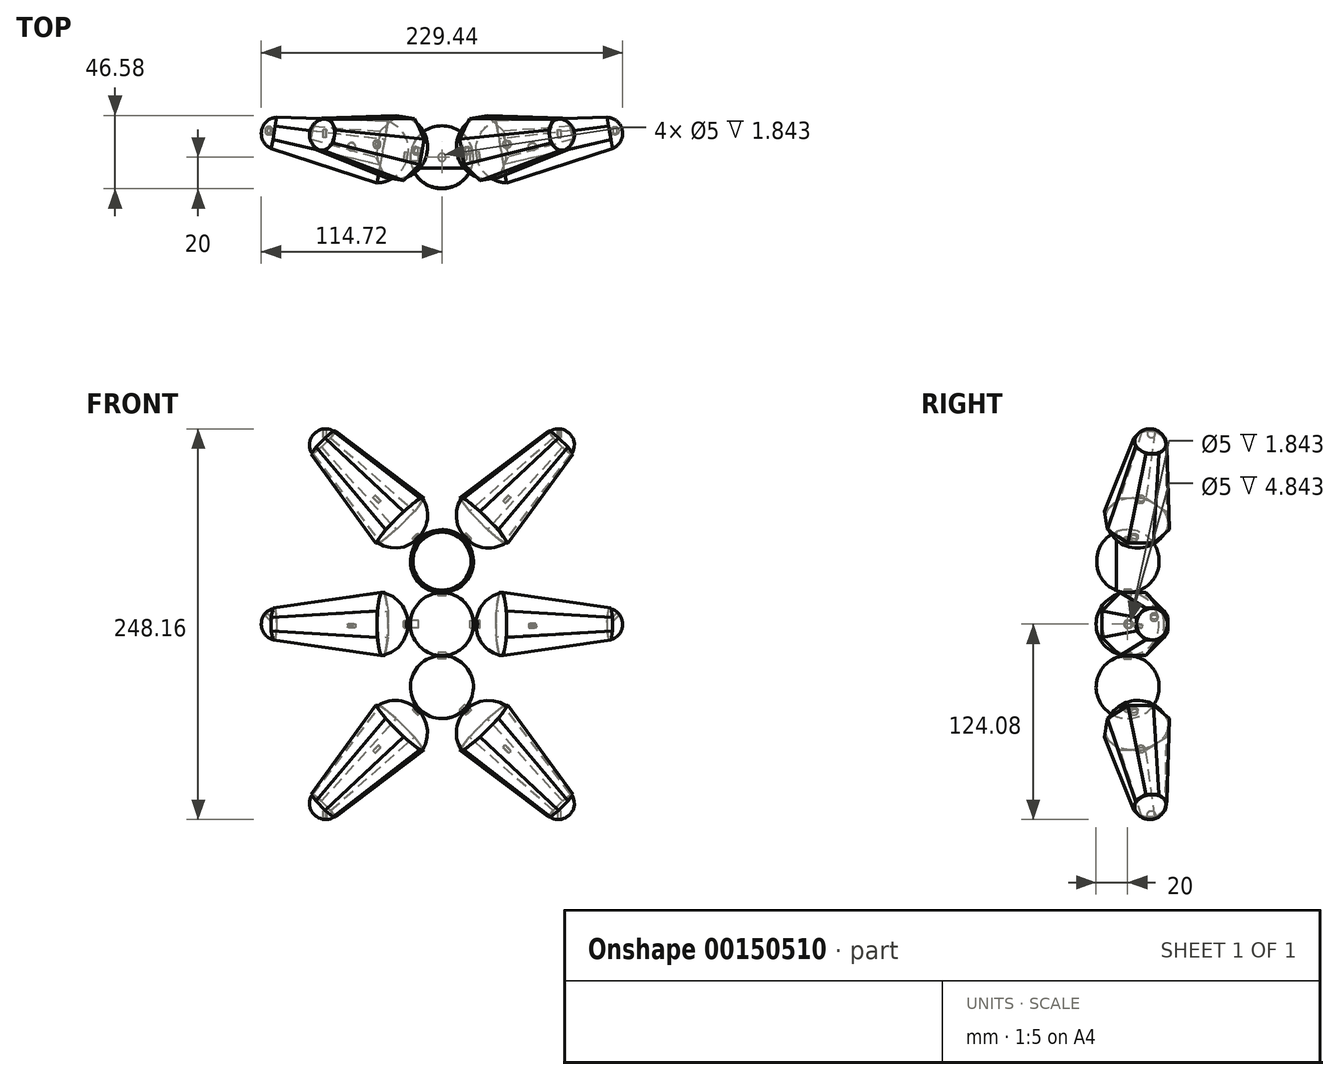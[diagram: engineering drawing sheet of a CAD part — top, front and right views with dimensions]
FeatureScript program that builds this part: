
annotation { "Feature Type Name" : "Feature", "Feature Type Description" : "" }
export const myFeature = defineFeature(function(context is Context, id is Id, definition is map)
    precondition{}
    {
        {
            var Q0;
            Q0=qCreatedBy(makeId("Top.planeOp"),FACE);
            var sketch = newSketch(context, id + "F0", { "sketchPlane" : qUnion([Q0])});
            skCircle(sketch, "E0", {"center": v(0, 0) * mm, "radius": 20 * mm});
            skCircle(sketch, "E1.cCircle", {"center": v(0, 0) * mm, "radius": 20 * mm, "construction": true});
            skLineSegment(sketch, "E1.0", {"start": v(18.28, 11.6) * mm, "end": v(21.13, -4.72) * mm});
            skLineSegment(sketch, "E1.1", {"start": v(21.13, -4.72) * mm, "end": v(11.6, -18.28) * mm});
            skLineSegment(sketch, "E1.2", {"start": v(11.6, -18.28) * mm, "end": v(-4.72, -21.13) * mm});
            skLineSegment(sketch, "E1.3", {"start": v(-4.72, -21.13) * mm, "end": v(-18.28, -11.6) * mm});
            skLineSegment(sketch, "E1.4", {"start": v(-18.28, -11.6) * mm, "end": v(-21.13, 4.72) * mm});
            skLineSegment(sketch, "E1.5", {"start": v(-21.13, 4.72) * mm, "end": v(-11.6, 18.28) * mm});
            skLineSegment(sketch, "E1.6", {"start": v(-11.6, 18.28) * mm, "end": v(4.72, 21.13) * mm});
            skLineSegment(sketch, "E1.7", {"start": v(4.72, 21.13) * mm, "end": v(18.28, 11.6) * mm});
            skPoint(sketch, "E1.0.midPoint", {"position": v(19.7, 3.44) * mm});
            skSolve(sketch);
        }
        {
            var Q0;
            {var subQ0=sQuery(id+"F0.wireOp",EDGE,"E0");var subQ4=makeQuery(id+"F0.imprint","INTERSECT",VERTEX,{"derivedFrom":[subQ0,sQuery(id+"F0.wireOp",EDGE,"E1.7")]});Q0=makeQuery(id+"F0.imprint","IMPRINT",FACE,{"disambiguationData":[TD([[makeQuery(id+"F0.imprint","IMPRINT",EDGE,{"disambiguationData":[TD([[subQ4,1.0]])],"derivedFrom":subQ0}),1.0]])]});}
            extrude(context, id + "F1", {"entities" : qUnion([Q0]), "oppositeDirection" : true, "depth" : 16 * mm});
        }
        {
            var Q0;
            {var subQ0=sQuery(id+"F0.wireOp",EDGE,"E0");var subQ4=makeQuery(id+"F0.imprint","INTERSECT",VERTEX,{"derivedFrom":[subQ0,sQuery(id+"F0.wireOp",EDGE,"E1.7")]});Q0=makeQuery(id+"F0.imprint","IMPRINT",FACE,{"disambiguationData":[TD([[makeQuery(id+"F0.imprint","IMPRINT",EDGE,{"disambiguationData":[TD([[subQ4,1.0]])],"derivedFrom":subQ0}),1.0]])]});}
            var Q1;
            {var subQ0=sQuery(id+"F0.wireOp",EDGE,"E1.7");var subQ1=sQuery(id+"F0.wireOp",EDGE,"E0");var subQ2=makeQuery(id+"F0.imprint","INTERSECT",VERTEX,{"derivedFrom":[subQ1,subQ0]});Q1=makeQuery(id+"F0.imprint","IMPRINT",FACE,{"disambiguationData":[TD([[makeQuery(id+"F0.imprint","IMPRINT",EDGE,{"disambiguationData":[TD([[subQ2,-1.0]])],"derivedFrom":subQ1}),-1.0]])]});}
            var Q2;
            {var subQ0=sQuery(id+"F0.wireOp",EDGE,"E1.7");var subQ1=sQuery(id+"F0.wireOp",EDGE,"E0");var subQ2=makeQuery(id+"F0.imprint","INTERSECT",VERTEX,{"derivedFrom":[subQ1,subQ0]});Q2=makeQuery(id+"F0.imprint","IMPRINT",FACE,{"disambiguationData":[TD([[makeQuery(id+"F0.imprint","IMPRINT",EDGE,{"disambiguationData":[TD([[subQ2,1.0]])],"derivedFrom":subQ1}),-1.0]])]});}
            var Q3;
            {var subQ0=sQuery(id+"F0.wireOp",EDGE,"E1.0");var subQ1=sQuery(id+"F0.wireOp",EDGE,"E0");var subQ2=makeQuery(id+"F0.imprint","INTERSECT",VERTEX,{"derivedFrom":[subQ1,subQ0]});Q3=makeQuery(id+"F0.imprint","IMPRINT",FACE,{"disambiguationData":[TD([[makeQuery(id+"F0.imprint","IMPRINT",EDGE,{"disambiguationData":[TD([[subQ2,1.0]])],"derivedFrom":subQ1}),-1.0]])]});}
            var Q4;
            {var subQ0=sQuery(id+"F0.wireOp",EDGE,"E1.2");var subQ1=sQuery(id+"F0.wireOp",EDGE,"E0");var subQ2=makeQuery(id+"F0.imprint","INTERSECT",VERTEX,{"derivedFrom":[subQ1,subQ0]});Q4=makeQuery(id+"F0.imprint","IMPRINT",FACE,{"disambiguationData":[TD([[makeQuery(id+"F0.imprint","IMPRINT",EDGE,{"disambiguationData":[TD([[subQ2,-1.0]])],"derivedFrom":subQ1}),-1.0]])]});}
            var Q5;
            {var subQ0=sQuery(id+"F0.wireOp",EDGE,"E1.3");var subQ1=sQuery(id+"F0.wireOp",EDGE,"E0");var subQ2=makeQuery(id+"F0.imprint","INTERSECT",VERTEX,{"derivedFrom":[subQ1,subQ0]});Q5=makeQuery(id+"F0.imprint","IMPRINT",FACE,{"disambiguationData":[TD([[makeQuery(id+"F0.imprint","IMPRINT",EDGE,{"disambiguationData":[TD([[subQ2,-1.0]])],"derivedFrom":subQ1}),-1.0]])]});}
            var Q6;
            {var subQ0=sQuery(id+"F0.wireOp",EDGE,"E1.4");var subQ1=sQuery(id+"F0.wireOp",EDGE,"E0");var subQ2=makeQuery(id+"F0.imprint","INTERSECT",VERTEX,{"derivedFrom":[subQ1,subQ0]});Q6=makeQuery(id+"F0.imprint","IMPRINT",FACE,{"disambiguationData":[TD([[makeQuery(id+"F0.imprint","IMPRINT",EDGE,{"disambiguationData":[TD([[subQ2,-1.0]])],"derivedFrom":subQ1}),-1.0]])]});}
            var Q7;
            {var subQ0=sQuery(id+"F0.wireOp",EDGE,"E1.5");var subQ1=sQuery(id+"F0.wireOp",EDGE,"E0");var subQ2=makeQuery(id+"F0.imprint","INTERSECT",VERTEX,{"derivedFrom":[subQ1,subQ0]});Q7=makeQuery(id+"F0.imprint","IMPRINT",FACE,{"disambiguationData":[TD([[makeQuery(id+"F0.imprint","IMPRINT",EDGE,{"disambiguationData":[TD([[subQ2,-1.0]])],"derivedFrom":subQ1}),-1.0]])]});}
            var Q8;
            {var subQ0=sQuery(id+"F0.wireOp",EDGE,"E1.6");var subQ1=sQuery(id+"F0.wireOp",EDGE,"E0");var subQ2=makeQuery(id+"F0.imprint","INTERSECT",VERTEX,{"derivedFrom":[subQ1,subQ0]});Q8=makeQuery(id+"F0.imprint","IMPRINT",FACE,{"disambiguationData":[TD([[makeQuery(id+"F0.imprint","IMPRINT",EDGE,{"disambiguationData":[TD([[subQ2,-1.0]])],"derivedFrom":subQ1}),-1.0]])]});}
            extrude(context, id + "F2", {"entities" : qUnion([Q0, Q1, Q2, Q3, Q4, Q5, Q6, Q7, Q8]), "operationType" : NewBodyOperationType.ADD, "depth" : 70 * mm, "hasDraft" : true, "draftAngle" : 8 * degree, "draftPullDirection" : true});
        }
        {
            var Q0;
            Q0=makeQuery(id+"F1.opExtrude","CAP_EDGE",EDGE,{"disambiguationData":[OSD([sQuery(id+"F0.wireOp",EDGE,"E0")])],"isStart":false});
            fillet(context, id + "F3", {"entities" : qUnion([Q0]), "radius" : 20 * mm, "tangentPropagation" : true, "allowEdgeOverflow" : false});
        }
        {
            var Q0;
            Q0=makeQuery(id+"F2.opExtrude","CAP_FACE",FACE,{"disambiguationData":[OSD([sQuery(id+"F0.wireOp",EDGE,"E1.0"),sQuery(id+"F0.wireOp",EDGE,"E1.1"),sQuery(id+"F0.wireOp",EDGE,"E1.2"),sQuery(id+"F0.wireOp",EDGE,"E1.3"),sQuery(id+"F0.wireOp",EDGE,"E1.4"),sQuery(id+"F0.wireOp",EDGE,"E1.5"),sQuery(id+"F0.wireOp",EDGE,"E1.6"),sQuery(id+"F0.wireOp",EDGE,"E1.7")])],"isStart":false});
            var sketch = newSketch(context, id + "F4", { "sketchPlane" : qUnion([Q0])});
            skCircle(sketch, "E2", {"center": v(0, 0) * mm, "radius": 10 * mm});
            skSolve(sketch);
        }
        {
            var Q0;
            Q0=makeQuery(id+"F4.imprint","IMPRINT",FACE,{"disambiguationData":[TD([[makeQuery(id+"F4.imprint","IMPRINT",EDGE,{"derivedFrom":sQuery(id+"F4.wireOp",EDGE,"E2")}),1.0]])]});
            extrude(context, id + "F5", {"entities" : qUnion([Q0]), "operationType" : NewBodyOperationType.ADD, "depth" : 8 * mm});
        }
        {
            var Q0;
            Q0=makeQuery(id+"F5.opExtrude","CAP_EDGE",EDGE,{"disambiguationData":[OSD([sQuery(id+"F4.wireOp",EDGE,"E2")])],"isStart":false});
            fillet(context, id + "F6", {"entities" : qUnion([Q0]), "radius" : 10 * mm, "tangentPropagation" : true, "allowEdgeOverflow" : false});
        }
        {
            var Q0;
            Q0=makeQuery(id+"F1.opExtrude","CAP_FACE",FACE,{"disambiguationData":[OSD([sQuery(id+"F0.wireOp",EDGE,"E0")])],"isStart":false});
            var sketch = newSketch(context, id + "F7", { "sketchPlane" : qUnion([Q0])});
            skCircle(sketch, "E3", {"center": v(0, 0) * mm, "radius": 2.5 * mm});
            skSolve(sketch);
        }
        {
            var Q0;
            Q0 = qSketchRegion(id + "F7", true);
            extrude(context, id + "F8", {"entities" : qUnion([Q0]), "operationType" : NewBodyOperationType.REMOVE, "oppositeDirection" : true, "depth" : 2 * mm});
        }
        {
            var Q0;
            {var subQ0=sQuery(id+"F0.wireOp",EDGE,"E0");var subQ4=makeQuery(id+"F0.imprint","INTERSECT",VERTEX,{"derivedFrom":[subQ0,sQuery(id+"F0.wireOp",EDGE,"E1.7")]});Q0=makeQuery(id+"F0.imprint","IMPRINT",FACE,{"disambiguationData":[TD([[makeQuery(id+"F0.imprint","IMPRINT",EDGE,{"disambiguationData":[TD([[subQ4,1.0]])],"derivedFrom":subQ0}),1.0]])]});}
            extrude(context, id + "F9", {"entities" : qUnion([Q0]), "endBound" : BoundingType.SYMMETRIC, "depth" : 40 * mm});
        }
        {
            var Q0;
            Q0=makeQuery(id+"F9.opExtrude","CAP_EDGE",EDGE,{"disambiguationData":[OSD([sQuery(id+"F0.wireOp",EDGE,"E0")])],"isStart":false});
            var Q1;
            Q1=makeQuery(id+"F9.opExtrude","CAP_EDGE",EDGE,{"disambiguationData":[OSD([sQuery(id+"F0.wireOp",EDGE,"E0")])],"isStart":true});
            fillet(context, id + "F10", {"entities" : qUnion([Q0, Q1]), "radius" : 20 * mm, "tangentPropagation" : true, "allowEdgeOverflow" : false});
        }
        {
            var Q0;
            Q0=makeQuery(id+"F1.opExtrude","SWEPT_BODY",BODY,{"disambiguationData":[OSD([sQuery(id+"F0.wireOp",EDGE,"E0")])]});
            transform(context, id + "F11", {"entities" : qUnion([Q0]), "transformType" : TransformType.TRANSLATION_3D, "dx" : 18 * mm, "dy" : 0 * mm, "dz" : -20 * mm, "makeCopy" : false});
        }
        {
            var Q0;
            Q0=makeQuery(id+"F9.opExtrude","SWEPT_BODY",BODY,{"disambiguationData":[OSD([sQuery(id+"F0.wireOp",EDGE,"E0")])]});
            transform(context, id + "F12", {"entities" : qUnion([Q0]), "transformType" : TransformType.TRANSLATION_3D, "dx" : 0 * mm, "dy" : 0 * mm, "dz" : 40 * mm, "makeCopy" : false});
        }
        {
            var Q0;
            Q0=qCreatedBy(makeId("Top.planeOp"),FACE);
            cPlane(context, id + "F13", {"entities" : qUnion([Q0]), "cplaneType" : CPlaneType.OFFSET, "offset" : 20 * mm, "width" : 150 * mm, "height" : 150 * mm});
        }
        {
            var Q0;
            Q0=qCreatedBy(id+"F13.planeOp",FACE);
            var sketch = newSketch(context, id + "F14", { "sketchPlane" : qUnion([Q0])});
            skCircle(sketch, "E4", {"center": v(0, 0) * mm, "radius": 2.5 * mm});
            skSolve(sketch);
        }
        {
            var Q0;
            Q0 = qSketchRegion(id + "F14", true);
            extrude(context, id + "F15", {"entities" : qUnion([Q0]), "operationType" : NewBodyOperationType.REMOVE, "depth" : 2 * mm});
        }
        {
            var Q0;
            Q0=makeQuery(id+"F9.opExtrude","SWEPT_BODY",BODY,{"disambiguationData":[OSD([sQuery(id+"F0.wireOp",EDGE,"E0")])]});
            transform(context, id + "F16", {"entities" : qUnion([Q0]), "transformType" : TransformType.TRANSLATION_3D, "dx" : 0 * mm, "dy" : 0 * mm, "dz" : -40 * mm, "makeCopy" : true});
        }
        {
            var Q0;
            Q0=qCreatedBy(makeId("Front.planeOp"),FACE);
            var sketch = newSketch(context, id + "F17", { "sketchPlane" : qUnion([Q0])});
            skLineSegment(sketch, "E5", {"start": v(0, 68.28) * mm, "end": v(-28.28, 40) * mm});
            skLineSegment(sketch, "E6", {"start": v(-28.28, 40) * mm, "end": v(0, 11.72) * mm});
            skLineSegment(sketch, "E7", {"start": v(0, 11.72) * mm, "end": v(28.28, 40) * mm});
            skLineSegment(sketch, "E8", {"start": v(28.28, 40) * mm, "end": v(0, 68.28) * mm});
            skLineSegment(sketch, "E9", {"start": v(0, 0) * mm, "end": v(0, 68.28) * mm, "construction": true});
            skLineSegment(sketch, "E10", {"start": v(-28.28, 40) * mm, "end": v(28.28, 40) * mm, "construction": true});
            skSolve(sketch);
        }
        {
            var Q0;
            Q0=sQuery(id+"F17.wireOp",EDGE,"E5");
            cPlane(context, id + "F18", {"entities" : qUnion([Q0]), "cplaneType" : CPlaneType.LINE_ANGLE, "offset" : 25 * mm, "angle" : 90 * degree, "width" : 150 * mm, "height" : 150 * mm});
        }
        {
            var Q0;
            Q0=qCreatedBy(id+"F18.planeOp",FACE);
            var sketch = newSketch(context, id + "F19", { "sketchPlane" : qUnion([Q0])});
            skCircle(sketch, "E11", {"center": v(28.28, 0) * mm, "radius": 2.5 * mm});
            skSolve(sketch);
        }
        {
            var Q0;
            Q0 = qSketchRegion(id + "F19", true);
            extrude(context, id + "F20", {"entities" : qUnion([Q0]), "operationType" : NewBodyOperationType.REMOVE, "oppositeDirection" : true, "depth" : 2 * mm});
        }
        {
            var Q0;
            Q0=sQuery(id+"F17.wireOp",EDGE,"E8");
            cPlane(context, id + "F21", {"entities" : qUnion([Q0]), "cplaneType" : CPlaneType.LINE_ANGLE, "offset" : 25 * mm, "angle" : 90 * degree, "width" : 150 * mm, "height" : 150 * mm});
        }
        {
            var Q0;
            Q0=qCreatedBy(id+"F21.planeOp",FACE);
            var sketch = newSketch(context, id + "F22", { "sketchPlane" : qUnion([Q0])});
            skCircle(sketch, "E12", {"center": v(0, 28.28) * mm, "radius": 2.5 * mm});
            skSolve(sketch);
        }
        {
            var Q0;
            Q0 = qSketchRegion(id + "F22", true);
            extrude(context, id + "F23", {"entities" : qUnion([Q0]), "operationType" : NewBodyOperationType.REMOVE, "oppositeDirection" : true, "depth" : 2 * mm});
        }
        {
            var Q0;
            Q0=makeQuery(id+"F9.opExtrude","SWEPT_BODY",BODY,{"disambiguationData":[OSD([sQuery(id+"F0.wireOp",EDGE,"E0")])]});
            var Q1;
            Q1=qCreatedBy(makeId("Top.planeOp"),FACE);
            mirror(context, id + "F24", {"entities" : qUnion([Q0]), "mirrorPlane" : qUnion([Q1])});
        }
        {
            var Q0;
            Q0 = qSketchRegion(id + "F14", true);
            extrude(context, id + "F25", {"entities" : qUnion([Q0]), "operationType" : NewBodyOperationType.REMOVE, "oppositeDirection" : true, "depth" : 2 * mm});
        }
        {
            var Q0;
            Q0=qCreatedBy(makeId("Right.planeOp"),FACE);
            cPlane(context, id + "F26", {"entities" : qUnion([Q0]), "cplaneType" : CPlaneType.OFFSET, "offset" : 20 * mm, "width" : 150 * mm, "height" : 150 * mm});
        }
        {
            var Q0;
            Q0=qCreatedBy(id+"F26.planeOp",FACE);
            var sketch = newSketch(context, id + "F27", { "sketchPlane" : qUnion([Q0])});
            skCircle(sketch, "E13", {"center": v(0, 0) * mm, "radius": 2.5 * mm});
            skSolve(sketch);
        }
        {
            var Q0;
            Q0 = qSketchRegion(id + "F27", true);
            extrude(context, id + "F28", {"entities" : qUnion([Q0]), "operationType" : NewBodyOperationType.REMOVE, "oppositeDirection" : true, "depth" : 2 * mm});
        }
        {
            var Q0;
            Q0=qCreatedBy(makeId("Right.planeOp"),FACE);
            cPlane(context, id + "F29", {"entities" : qUnion([Q0]), "cplaneType" : CPlaneType.OFFSET, "offset" : 20 * mm, "oppositeDirection" : true, "width" : 150 * mm, "height" : 150 * mm});
        }
        {
            var Q0;
            Q0=qCreatedBy(id+"F29.planeOp",FACE);
            var sketch = newSketch(context, id + "F30", { "sketchPlane" : qUnion([Q0])});
            skCircle(sketch, "E14", {"center": v(0, 0) * mm, "radius": 2.5 * mm});
            skSolve(sketch);
        }
        {
            var Q0;
            Q0 = qSketchRegion(id + "F30", true);
            extrude(context, id + "F31", {"entities" : qUnion([Q0]), "operationType" : NewBodyOperationType.REMOVE, "depth" : 5 * mm});
        }
        {
            var Q0;
            Q0=qCreatedBy(makeId("Front.planeOp"),FACE);
            cPlane(context, id + "F32", {"entities" : qUnion([Q0]), "cplaneType" : CPlaneType.OFFSET, "offset" : 7 * mm, "width" : 150 * mm, "height" : 150 * mm});
        }
        {
            var Q0;
            Q0=qCreatedBy(id+"F32.planeOp",FACE);
            var sketch = newSketch(context, id + "F33", { "sketchPlane" : qUnion([Q0])});
            skCircle(sketch, "E15", {"center": v(0, 40) * mm, "radius": 19 * mm});
            skSolve(sketch);
        }
        {
            var Q0;
            Q0=makeQuery(id+"F33.imprint","IMPRINT",FACE,{"disambiguationData":[TD([[makeQuery(id+"F33.imprint","IMPRINT",EDGE,{"derivedFrom":sQuery(id+"F33.wireOp",EDGE,"E15")}),1.0]])]});
            extrude(context, id + "F34", {"entities" : qUnion([Q0]), "depth" : (20 - 7) * mm});
        }
        {
            var Q0;
            Q0=makeQuery(id+"F34.opExtrude","CAP_EDGE",EDGE,{"disambiguationData":[OSD([sQuery(id+"F33.wireOp",EDGE,"E15")])],"isStart":false});
            fillet(context, id + "F35", {"entities" : qUnion([Q0]), "radius" : 19 * mm, "tangentPropagation" : true, "allowEdgeOverflow" : false});
        }
        {
            var Q0;
            Q0=makeQuery(id+"F34.opExtrude","CAP_FACE",FACE,{"disambiguationData":[OSD([sQuery(id+"F33.wireOp",EDGE,"E15")])],"isStart":true});
            shell(context, id + "F36", {"entities" : qUnion([Q0]), "thickness" : .5 * mm});
        }
        {
            var Q0;
            Q0=makeQuery(id+"F34.opExtrude","SWEPT_BODY",BODY,{"disambiguationData":[OSD([sQuery(id+"F33.wireOp",EDGE,"E15")])]});
            var Q1;
            Q1=makeQuery(id+"F9.opExtrude","SWEPT_BODY",BODY,{"disambiguationData":[OSD([sQuery(id+"F0.wireOp",EDGE,"E0")])]});
            booleanBodies(context, id + "F37", {"operationType" : BooleanOperationType.SUBTRACTION, "tools" : qUnion([Q0]), "targets" : qUnion([Q1])});
        }
        {
            var Q0;
            Q0=makeQuery(id+"F1.opExtrude","SWEPT_BODY",BODY,{"disambiguationData":[OSD([sQuery(id+"F0.wireOp",EDGE,"E0")])]});
            var Q1;
            {var subQ0=sQuery(id+"F0.wireOp",EDGE,"E1.2");var subQ1=sQuery(id+"F0.wireOp",EDGE,"E1.3");Q1=makeQuery(id+"F2.boolean.opBoolean","SPLIT",EDGE,{"disambiguationData":[TD([makeQuery(id+"F2.opExtrude","SWEPT_FACE",FACE,{"disambiguationData":[OSD([subQ1])]})])],"derivedFrom":makeQuery(id+"F2.opExtrude","CAP_EDGE",EDGE,{"disambiguationData":[OSD([subQ0])],"isStart":true})});}
            var Q2;
            {var subQ0=sQuery(id+"F0.wireOp",EDGE,"E1.0");var subQ1=sQuery(id+"F0.wireOp",EDGE,"E1.7");Q2=makeQuery(id+"F2.boolean.opBoolean","SPLIT",EDGE,{"disambiguationData":[TD([makeQuery(id+"F2.opExtrude","SWEPT_FACE",FACE,{"disambiguationData":[OSD([subQ1])]})])],"derivedFrom":makeQuery(id+"F2.opExtrude","CAP_EDGE",EDGE,{"disambiguationData":[OSD([subQ0])],"isStart":true})});}
            transform(context, id + "F38", {"entities" : qUnion([Q0]), "transformType" : TransformType.ROTATION, "transformAxis" : qUnion([Q2]), "angle" : 90 * degree, "oppositeDirection" : true, "makeCopy" : false});
        }
        {
            var Q0;
            Q0=makeQuery(id+"F1.opExtrude","SWEPT_BODY",BODY,{"disambiguationData":[OSD([sQuery(id+"F0.wireOp",EDGE,"E0")])]});
            var Q1;
            Q1=qCreatedBy(makeId("Right.planeOp"),FACE);
            mirror(context, id + "F39", {"entities" : qUnion([Q0]), "mirrorPlane" : qUnion([Q1])});
        }
        {
            var Q0;
            Q0=makeQuery(id+"F1.opExtrude","SWEPT_BODY",BODY,{"disambiguationData":[OSD([sQuery(id+"F0.wireOp",EDGE,"E0")])]});
            transform(context, id + "F40", {"entities" : qUnion([Q0]), "transformType" : TransformType.TRANSLATION_3D, "dx" : -25 * mm, "dy" : 0 * mm, "dz" : 60 * mm, "makeCopy" : true});
        }
        {
            var Q0;
            Q0=makeQuery(id+"F40.opPattern","COPY",BODY,{"derivedFrom":makeQuery(id+"F1.opExtrude","SWEPT_BODY",BODY,{"disambiguationData":[OSD([sQuery(id+"F0.wireOp",EDGE,"E0")])]}),"instanceName":"1"});
            var Q1;
            {var subQ0=sQuery(id+"F0.wireOp",EDGE,"E1.5");var subQ1=sQuery(id+"F0.wireOp",EDGE,"E1.4");Q1=makeQuery(id+"F40.opPattern","COPY",EDGE,{"derivedFrom":makeQuery(id+"F2.boolean.opBoolean","SPLIT",EDGE,{"disambiguationData":[TD([makeQuery(id+"F2.opExtrude","SWEPT_FACE",FACE,{"disambiguationData":[OSD([subQ0])]})])],"derivedFrom":makeQuery(id+"F2.opExtrude","CAP_EDGE",EDGE,{"disambiguationData":[OSD([subQ1])],"isStart":true})}),"instanceName":"1"});}
            transform(context, id + "F41", {"entities" : qUnion([Q0]), "transformType" : TransformType.ROTATION, "transformAxis" : qUnion([Q1]), "angle" : 45 * degree, "oppositeDirection" : true, "makeCopy" : false});
        }
        {
            var Q0;
            Q0=makeQuery(id+"F40.opPattern","COPY",BODY,{"derivedFrom":makeQuery(id+"F1.opExtrude","SWEPT_BODY",BODY,{"disambiguationData":[OSD([sQuery(id+"F0.wireOp",EDGE,"E0")])]}),"instanceName":"1"});
            var Q1;
            Q1=qCreatedBy(makeId("Right.planeOp"),FACE);
            mirror(context, id + "F42", {"entities" : qUnion([Q0]), "mirrorPlane" : qUnion([Q1])});
        }
        {
            var Q0;
            Q0=makeQuery(id+"F42.opPattern","COPY",BODY,{"derivedFrom":makeQuery(id+"F40.opPattern","COPY",BODY,{"derivedFrom":makeQuery(id+"F1.opExtrude","SWEPT_BODY",BODY,{"disambiguationData":[OSD([sQuery(id+"F0.wireOp",EDGE,"E0")])]}),"instanceName":"1"}),"instanceName":"1"});
            var Q1;
            Q1=makeQuery(id+"F40.opPattern","COPY",BODY,{"derivedFrom":makeQuery(id+"F1.opExtrude","SWEPT_BODY",BODY,{"disambiguationData":[OSD([sQuery(id+"F0.wireOp",EDGE,"E0")])]}),"instanceName":"1"});
            var Q2;
            Q2=qCreatedBy(makeId("Top.planeOp"),FACE);
            mirror(context, id + "F43", {"entities" : qUnion([Q0, Q1]), "mirrorPlane" : qUnion([Q2])});
        }
    });
